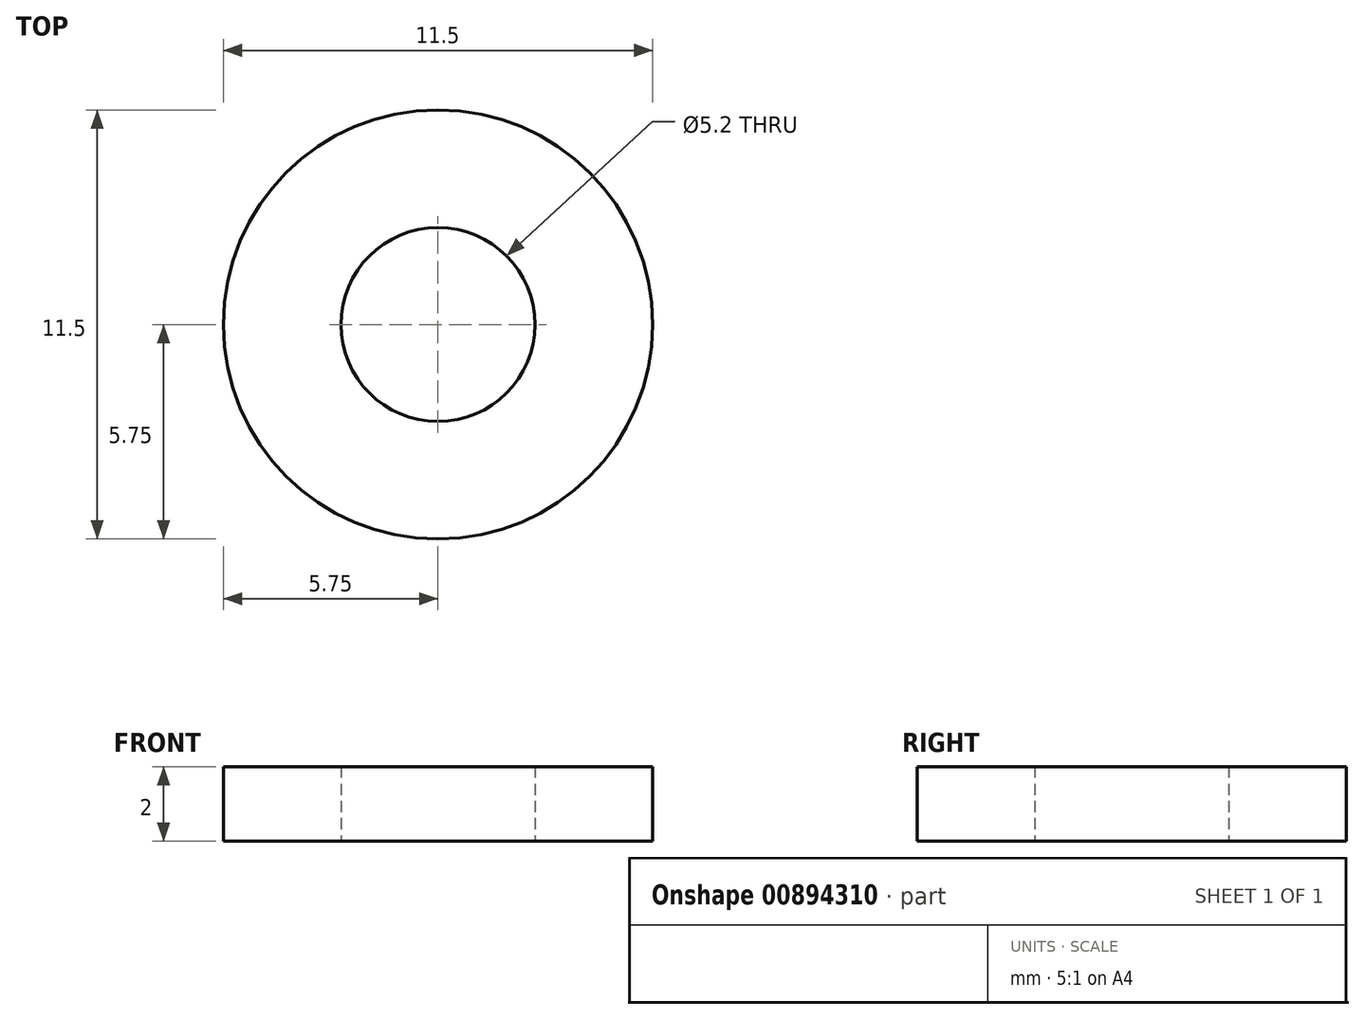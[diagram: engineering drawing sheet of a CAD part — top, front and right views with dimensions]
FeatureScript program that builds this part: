
annotation { "Feature Type Name" : "Feature", "Feature Type Description" : "" }
export const myFeature = defineFeature(function(context is Context, id is Id, definition is map)
    precondition{}
    {
        {
            var Q0;
            Q0=qCreatedBy(makeId("Top.planeOp"),FACE);
            var sketch = newSketch(context, id + "F0", { "sketchPlane" : qUnion([Q0])});
            skCircle(sketch, "E0", {"center": v(0, 0) * mm, "radius": 2.6 * mm});
            skCircle(sketch, "E1", {"center": v(0, 0) * mm, "radius": 5.75 * mm});
            skSolve(sketch);
        }
        {
            var Q0;
            Q0=makeQuery(id+"F0.imprint","IMPRINT",FACE,{"disambiguationData":[TD([[makeQuery(id+"F0.imprint","IMPRINT",EDGE,{"derivedFrom":sQuery(id+"F0.wireOp",EDGE,"E0")}),-1.0]])]});
            extrude(context, id + "F1", {"entities" : qUnion([Q0]), "depth" : 2 * mm, "offsetDistance" : 25 * mm});
        }
    });
